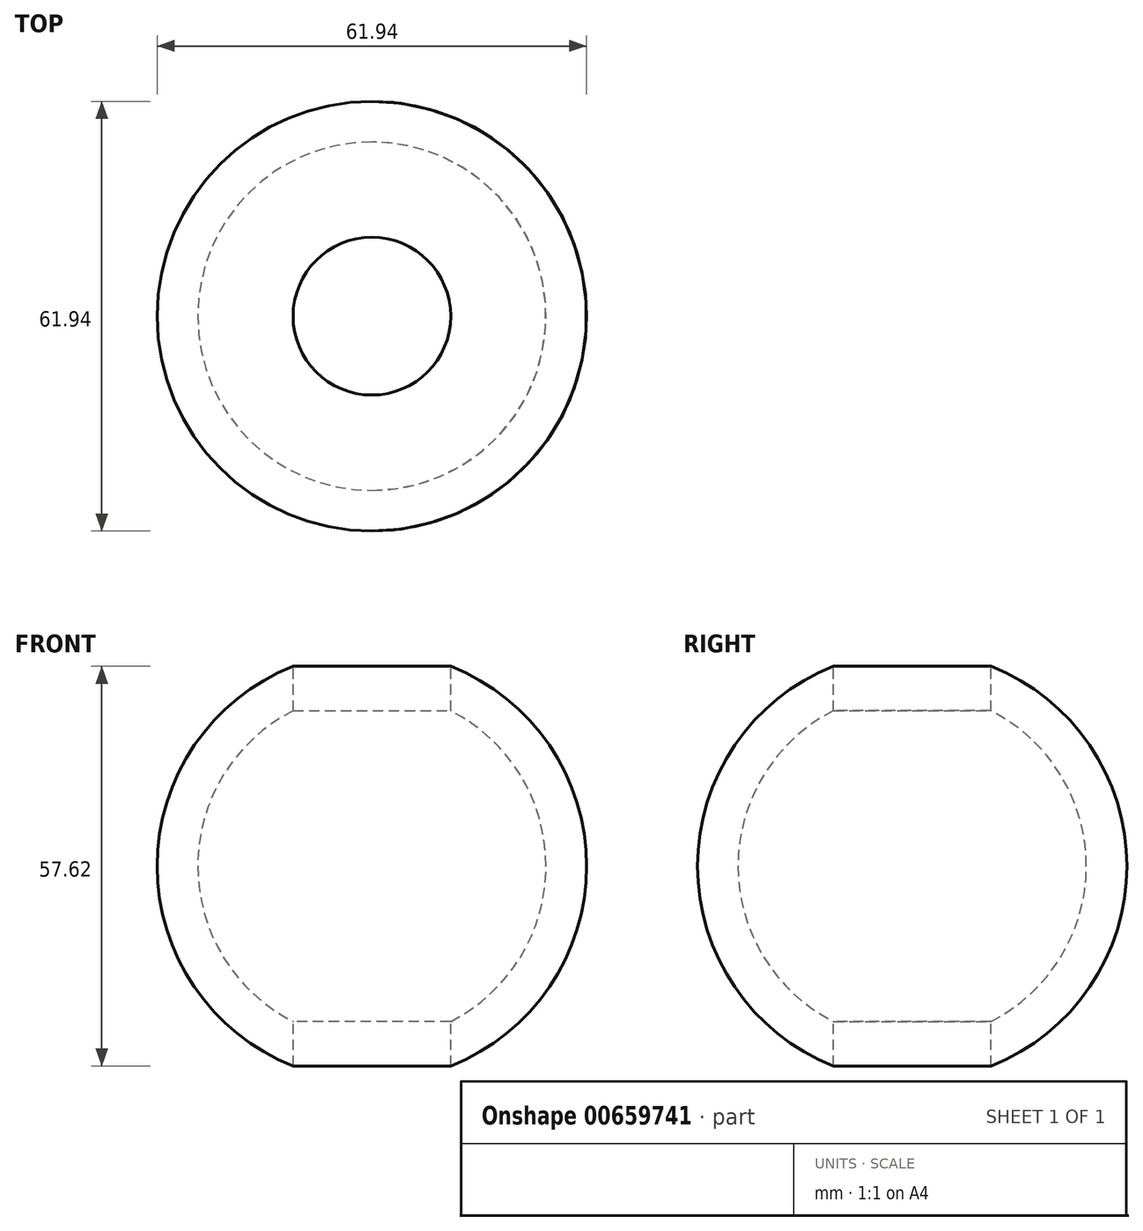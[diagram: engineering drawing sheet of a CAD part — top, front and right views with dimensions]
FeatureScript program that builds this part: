
annotation { "Feature Type Name" : "Feature", "Feature Type Description" : "" }
export const myFeature = defineFeature(function(context is Context, id is Id, definition is map)
    precondition{}
    {
        {
            var Q0;
            Q0=qCreatedBy(makeId("Top.planeOp"),FACE);
            var sketch = newSketch(context, id + "F0", { "sketchPlane" : qUnion([Q0])});
            skCircle(sketch, "E0", {"center": v(0, 0) * mm, "radius": 30.97 * mm});
            skCircle(sketch, "E1", {"center": v(0, 0) * mm, "radius": 25.12 * mm});
            skLineSegment(sketch, "E2", {"start": v(0, 40.44) * mm, "end": v(0, -45.62) * mm});
            skSolve(sketch);
        }
        {
            var Q0;
            {var subQ0=sQuery(id+"F0.wireOp",EDGE,"E2");var subQ1=sQuery(id+"F0.wireOp",EDGE,"E0");var subQ2=makeQuery(id+"F0.imprint","INTERSECT",VERTEX,{"disambiguationData":[OD(0.0)],"derivedFrom":[subQ1,subQ0]});Q0=makeQuery(id+"F0.imprint","IMPRINT",FACE,{"disambiguationData":[TD([[makeQuery(id+"F0.imprint","IMPRINT",EDGE,{"disambiguationData":[TD([[subQ2,-1.0]])],"derivedFrom":subQ1}),1.0]])]});}
            var Q1;
            Q1=sQuery(id+"F0.wireOp",EDGE,"E2");
            revolve(context, id + "F1", {"entities" : qUnion([Q0]), "axis" : qUnion([Q1]), "revolveType" : RevolveType.FULL});
        }
        {
            var Q0;
            Q0=qCreatedBy(makeId("Top.planeOp"),FACE);
            cPlane(context, id + "F2", {"entities" : qUnion([Q0]), "cplaneType" : CPlaneType.OFFSET, "offset" : 50.8 * mm, "width" : 152.4 * mm, "height" : 152.4 * mm});
        }
        {
            var Q0;
            Q0=qCreatedBy(id+"F2.planeOp",FACE);
            var sketch = newSketch(context, id + "F3", { "sketchPlane" : qUnion([Q0])});
            skCircle(sketch, "E3", {"center": v(0, 0) * mm, "radius": 11.37 * mm});
            skSolve(sketch);
        }
        {
            var Q0;
            Q0=makeQuery(id+"F3.imprint","IMPRINT",FACE,{"disambiguationData":[TD([[makeQuery(id+"F3.imprint","IMPRINT",EDGE,{"derivedFrom":sQuery(id+"F3.wireOp",EDGE,"E3")}),1.0]])]});
            extrude(context, id + "F4", {"entities" : qUnion([Q0]), "operationType" : NewBodyOperationType.REMOVE, "oppositeDirection" : true, "depth" : 101.6 * mm, "offsetDistance" : 25.4 * mm});
        }
    });
